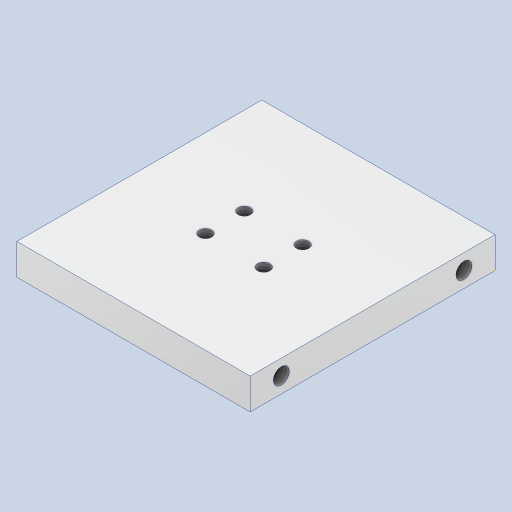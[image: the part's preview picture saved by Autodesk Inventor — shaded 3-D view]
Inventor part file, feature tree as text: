
AUTODESK INVENTOR PART (.ipt)
format: ipt  version: 2023 (Build 270158000, 158)  size: 148,480 bytes
history: native  units: mm
features: sketch x5, hole x3, extrude x1
ambient origin geometry x8: Origin, YZ Plane, XZ Plane, XY Plane, X Axis, Y Axis, Z Axis, Center Point
bodies: Solid1 (feature_tree)
feature tree (9):
  extrude  "Extrusion1"  Depth=63.0mm
  hole  "Furo1"  [1 undecoded]
  sketch  "Sketch3"  dims[d6=15.0mm d7=0.0mm]
  hole  "Hole2"  [1 undecoded]
  hole  "Hole3"  [1 undecoded]
  sketch  "Sketch1"  dims[d0=60.0mm d1=63.0mm]
  sketch  "Esboço2"  dims[d2=8.0mm d3=0.0mm d5=0.0mm]
  sketch  "Sketch4"  dims[d8=15.0mm d9=10.0mm]
  sketch  "Sketch5"  dims[d10=0.0mm d11=60.0mm d12=22.5mm d13=3.242mm d14=8.0mm d15=4.0mm d16=2.0mm d17=90.0deg d18=0.5mm d19=20.594885mm d20=26.0mm d21=8.0mm d22=8.0mm d23=4.134mm d24=10.0mm d25=4.0mm d26=2.0mm d27=90.0deg d28=14.2mm d29=20.594885mm d30=4.134mm d31=10.0mm d32=4.0mm d33=2.0mm d34=90.0deg d35=14.2mm d36=20.594885mm]
note: 3 required parameter values undecoded (feature->parameter linkage not recoverable at this tier; creation-order binding heuristic only, values carry confidence <= 0.55)
